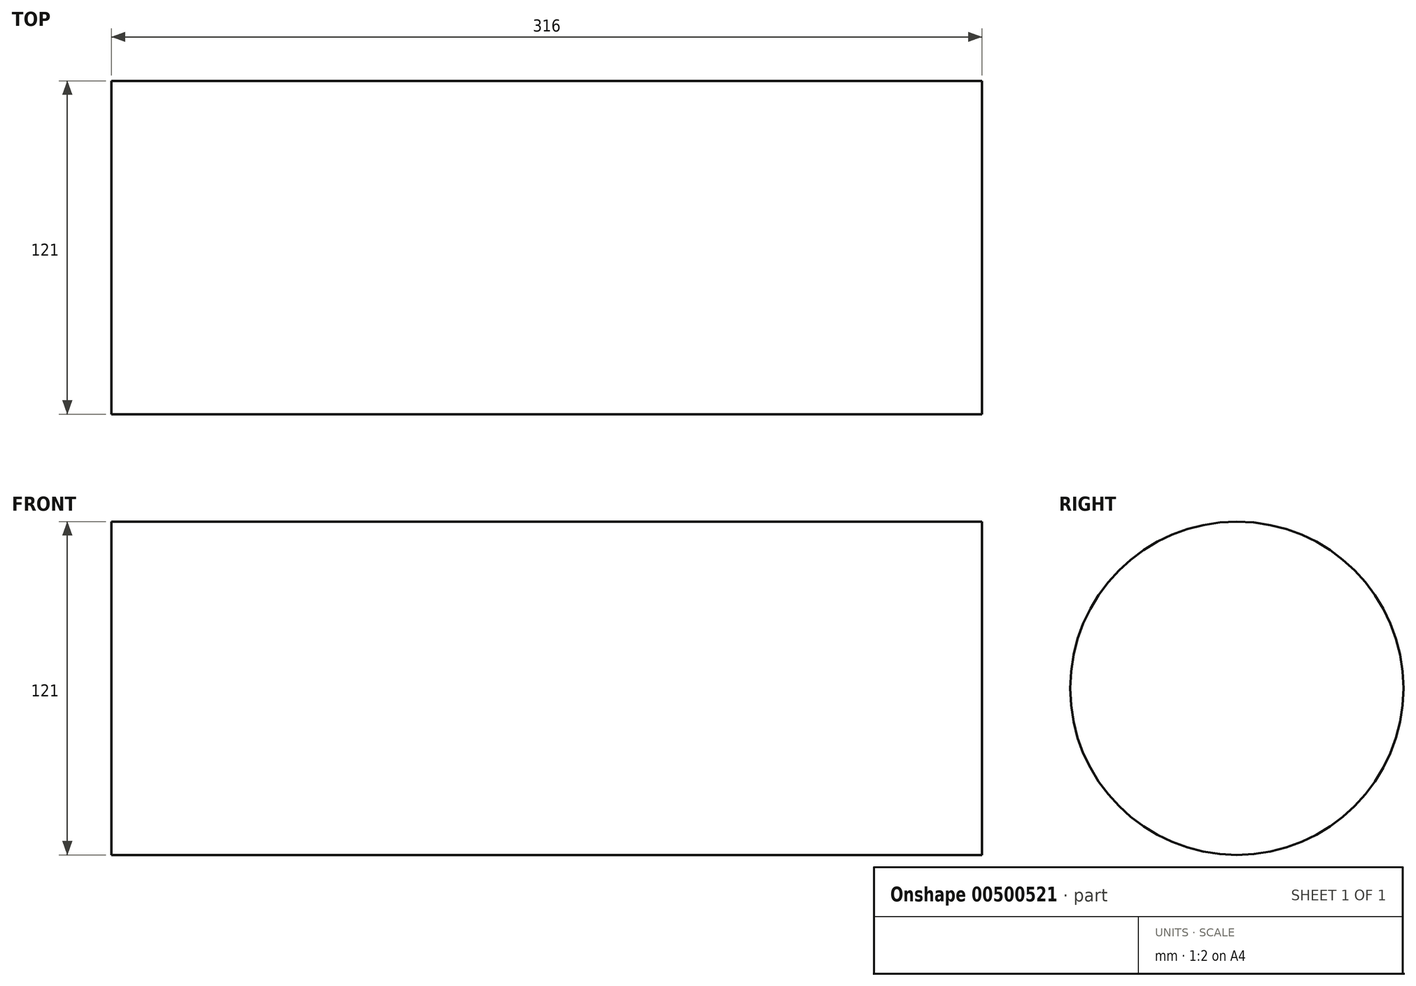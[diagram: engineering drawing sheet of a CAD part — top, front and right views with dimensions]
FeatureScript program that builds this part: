
annotation { "Feature Type Name" : "Feature", "Feature Type Description" : "" }
export const myFeature = defineFeature(function(context is Context, id is Id, definition is map)
    precondition{}
    {
        {
            var Q0;
            Q0=qCreatedBy(makeId("Right.planeOp"),FACE);
            var sketch = newSketch(context, id + "F0", { "sketchPlane" : qUnion([Q0])});
            skCircle(sketch, "E0", {"center": v(0, 0) * mm, "radius": 60.5 * mm});
            skSolve(sketch);
        }
        {
            var Q0;
            Q0=makeQuery(id+"F0.imprint","IMPRINT",FACE,{"disambiguationData":[TD([[makeQuery(id+"F0.imprint","IMPRINT",EDGE,{"derivedFrom":sQuery(id+"F0.wireOp",EDGE,"E0")}),1.0]])]});
            extrude(context, id + "F1", {"entities" : qUnion([Q0]), "depth" : 316 * mm});
        }
    });
